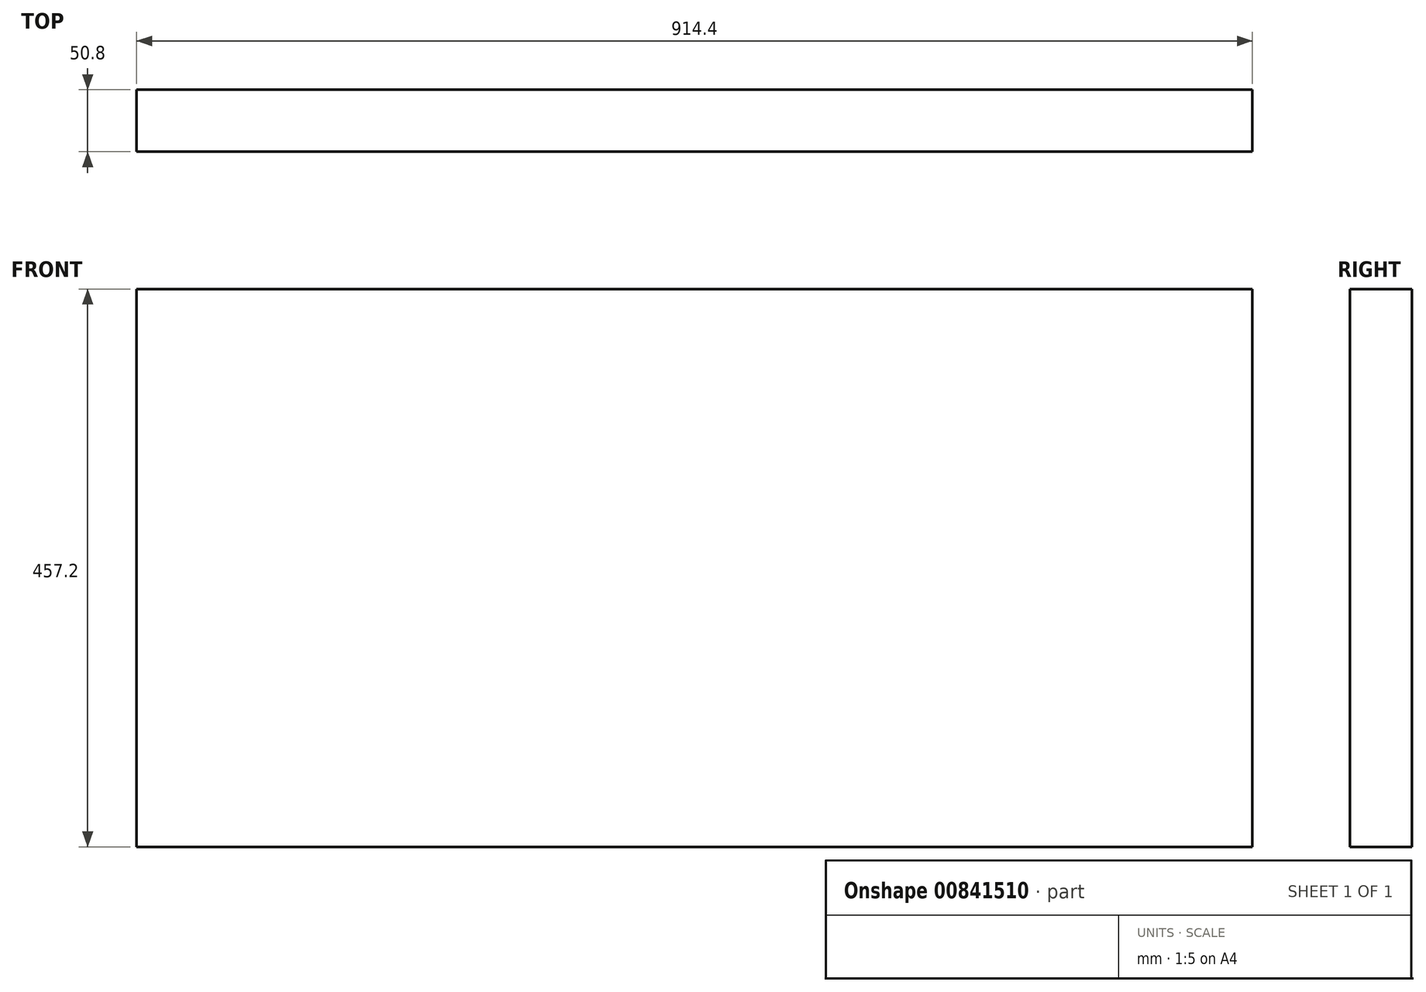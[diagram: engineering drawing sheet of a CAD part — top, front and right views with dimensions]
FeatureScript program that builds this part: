
annotation { "Feature Type Name" : "Feature", "Feature Type Description" : "" }
export const myFeature = defineFeature(function(context is Context, id is Id, definition is map)
    precondition{}
    {
        {
            var Q0;
            Q0=qCreatedBy(makeId("Right.planeOp"),FACE);
            var sketch = newSketch(context, id + "F0", { "sketchPlane" : qUnion([Q0])});
            skLineSegment(sketch, "E0.bottom", {"start": v(0, 0) * mm, "end": v(50.8, 0) * mm});
            skLineSegment(sketch, "E0.top", {"start": v(0, 457.2) * mm, "end": v(50.8, 457.2) * mm});
            skLineSegment(sketch, "E0.left", {"start": v(0, 0) * mm, "end": v(0, 457.2) * mm});
            skLineSegment(sketch, "E0.right", {"start": v(50.8, 0) * mm, "end": v(50.8, 457.2) * mm});
            skSolve(sketch);
        }
        {
            var Q0;
            Q0=qSketchRegion(id+"F0",true);
            extrude(context, id + "F1", {"entities" : qUnion([Q0]), "depth" : 914.4 * mm, "offsetDistance" : 25.4 * mm});
        }
    });
